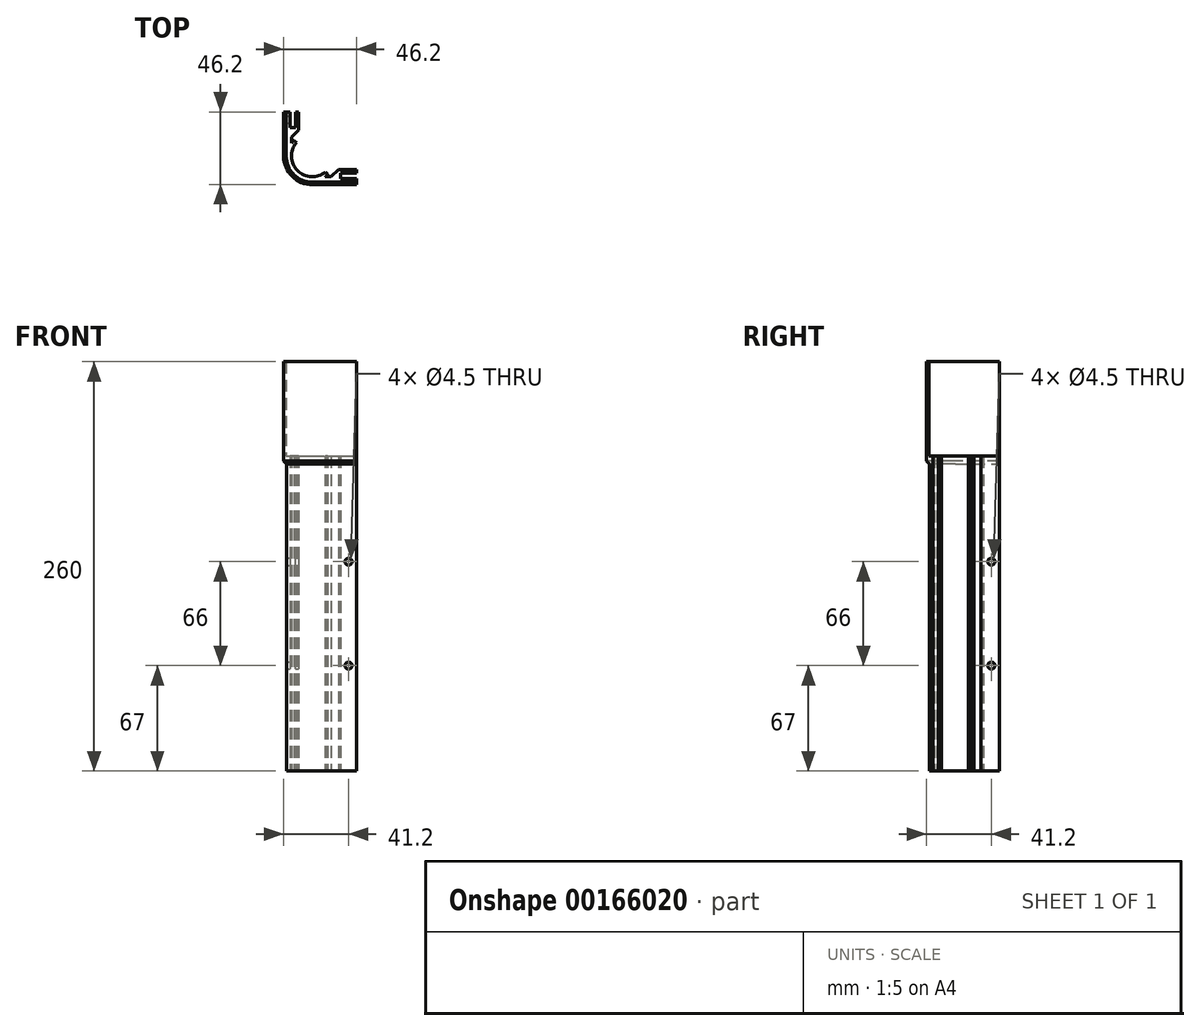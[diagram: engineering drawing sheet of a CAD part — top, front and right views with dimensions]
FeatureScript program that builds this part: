
annotation { "Feature Type Name" : "Feature", "Feature Type Description" : "" }
export const myFeature = defineFeature(function(context is Context, id is Id, definition is map)
    precondition{}
    {
        {
            var Q0;
            Q0=qCreatedBy(makeId("Top.planeOp"),FACE);
            var sketch = newSketch(context, id + "F0", { "sketchPlane" : qUnion([Q0])});
            skCircle(sketch, "E0", {"center": v(0, 0) * mm, "radius": 13.2 * mm, "construction": true});
            skArc(sketch, "E1", {"start": v(-16.2, 0) * mm, "mid": v(-11.46, -11.46) * mm, "end": v(0, -16.2) * mm});
            skLineSegment(sketch, "E2", {"start": v(-5.38, 20.06) * mm, "end": v(5.38, -20.06) * mm, "construction": true});
            skLineSegment(sketch, "E3", {"start": v(21.9, -5.87) * mm, "end": v(-21.9, 5.87) * mm, "construction": true});
            skPoint(sketch, "E4", {"position": v(-3.42, 12.75) * mm});
            skPoint(sketch, "E5", {"position": v(12.75, -3.42) * mm});
            skArc(sketch, "E6", {"start": v(0, -16.2) * mm, "mid": v(9.03, -12.45) * mm, "end": v(12.75, -3.42) * mm});
            skArc(sketch, "E7", {"start": v(-3.42, 12.75) * mm, "mid": v(-9.33, -9.33) * mm, "end": v(12.75, -3.42) * mm});
            skPoint(sketch, "E8", {"position": v(-13.2, 0) * mm});
            skPoint(sketch, "E9", {"position": v(0, -13.2) * mm});
            skArc(sketch, "E10", {"start": v(-16.2, 0) * mm, "mid": v(-12.45, 9.03) * mm, "end": v(-3.42, 12.75) * mm});
            skPoint(sketch, "E11", {"position": v(-11.46, -11.46) * mm});
            skLineSegment(sketch, "E12", {"start": v(-13.2, 0) * mm, "end": v(-13.2, 12) * mm});
            skLineSegment(sketch, "E13", {"start": v(-16.2, 0) * mm, "end": v(-16.2, 12) * mm});
            skLineSegment(sketch, "E14", {"start": v(0, -13.2) * mm, "end": v(12, -13.2) * mm});
            skLineSegment(sketch, "E15", {"start": v(0, -16.2) * mm, "end": v(12, -16.2) * mm});
            skLineSegment(sketch, "E16", {"start": v(-16.2, 12) * mm, "end": v(-16.2, 28) * mm});
            skLineSegment(sketch, "E17", {"start": v(-16.2, 28) * mm, "end": v(-14.2, 28) * mm});
            skLineSegment(sketch, "E18", {"start": v(-13.2, 12) * mm, "end": v(-8.7, 16.5) * mm});
            skLineSegment(sketch, "E19", {"start": v(-8.7, 16.5) * mm, "end": v(-8.7, 28) * mm});
            skLineSegment(sketch, "E20", {"start": v(-8.7, 28) * mm, "end": v(-10.7, 28) * mm});
            skLineSegment(sketch, "E21", {"start": v(-10.7, 28) * mm, "end": v(-10.7, 18) * mm});
            skLineSegment(sketch, "E22", {"start": v(-10.7, 18) * mm, "end": v(-14.2, 18) * mm});
            skLineSegment(sketch, "E23", {"start": v(-14.2, 18) * mm, "end": v(-14.2, 28) * mm});
            skLineSegment(sketch, "E24", {"start": v(0, 0) * mm, "end": v(-11.46, -11.46) * mm, "construction": true});
            skLineSegment(sketch, "E25.MirrorCS", {"start": v(12, -13.2) * mm, "end": v(16.5, -8.7) * mm});
            skLineSegment(sketch, "E26.MirrorCS", {"start": v(16.5, -8.7) * mm, "end": v(28, -8.7) * mm});
            skLineSegment(sketch, "E27.MirrorCS", {"start": v(28, -8.7) * mm, "end": v(28, -10.7) * mm});
            skLineSegment(sketch, "E28.MirrorCS", {"start": v(28, -10.7) * mm, "end": v(18, -10.7) * mm});
            skLineSegment(sketch, "E29.MirrorCS", {"start": v(18, -10.7) * mm, "end": v(18, -14.2) * mm});
            skLineSegment(sketch, "E30.MirrorCS", {"start": v(18, -14.2) * mm, "end": v(28, -14.2) * mm});
            skLineSegment(sketch, "E31.MirrorCS", {"start": v(28, -16.2) * mm, "end": v(28, -14.2) * mm});
            skLineSegment(sketch, "E32.MirrorCS", {"start": v(12, -16.2) * mm, "end": v(28, -16.2) * mm});
            skLineSegment(sketch, "E33", {"start": v(-10.7, 18) * mm, "end": v(15.7, 18) * mm, "construction": true});
            skLineSegment(sketch, "E34", {"start": v(0, 0) * mm, "end": v(0, 18) * mm, "construction": true});
            skSolve(sketch);
        }
        {
            var Q0;
            Q0 = qSketchRegion(id + "F0", true);
            extrude(context, id + "F1", {"entities" : qUnion([Q0]), "depth" : 200 * mm});
        }
        {
            var Q0;
            Q0=makeQuery(id+"F1.opExtrude","SWEPT_EDGE",EDGE,{"disambiguationData":[OSD([sQuery(id+"F0.wireOp",EDGE,"E7"),sQuery(id+"F0.wireOp",EDGE,"E10")])]});
            var Q1;
            Q1=makeQuery(id+"F1.opExtrude","SWEPT_EDGE",EDGE,{"disambiguationData":[OSD([sQuery(id+"F0.wireOp",EDGE,"E6"),sQuery(id+"F0.wireOp",EDGE,"E7")])]});
            chamfer(context, id + "F2", {"entities" : qUnion([Q0, Q1]), "width" : 1 * mm, "tangentPropagation" : true});
        }
        {
            var Q0;
            Q0=makeQuery(id+"F1.opExtrude","CAP_FACE",FACE,{"disambiguationData":[OSD([sQuery(id+"F0.wireOp",EDGE,"E1"),sQuery(id+"F0.wireOp",EDGE,"E6"),sQuery(id+"F0.wireOp",EDGE,"E7"),sQuery(id+"F0.wireOp",EDGE,"E10"),sQuery(id+"F0.wireOp",EDGE,"E12"),sQuery(id+"F0.wireOp",EDGE,"E13"),sQuery(id+"F0.wireOp",EDGE,"E14"),sQuery(id+"F0.wireOp",EDGE,"E15"),sQuery(id+"F0.wireOp",EDGE,"E16"),sQuery(id+"F0.wireOp",EDGE,"E17"),sQuery(id+"F0.wireOp",EDGE,"E18"),sQuery(id+"F0.wireOp",EDGE,"E19"),sQuery(id+"F0.wireOp",EDGE,"E20"),sQuery(id+"F0.wireOp",EDGE,"E21"),sQuery(id+"F0.wireOp",EDGE,"E22"),sQuery(id+"F0.wireOp",EDGE,"E23"),sQuery(id+"F0.wireOp",EDGE,"E25.MirrorCS"),sQuery(id+"F0.wireOp",EDGE,"E26.MirrorCS"),sQuery(id+"F0.wireOp",EDGE,"E27.MirrorCS"),sQuery(id+"F0.wireOp",EDGE,"E28.MirrorCS"),sQuery(id+"F0.wireOp",EDGE,"E29.MirrorCS"),sQuery(id+"F0.wireOp",EDGE,"E30.MirrorCS"),sQuery(id+"F0.wireOp",EDGE,"E31.MirrorCS"),sQuery(id+"F0.wireOp",EDGE,"E32.MirrorCS")])],"isStart":false});
            var sketch = newSketch(context, id + "F3", { "sketchPlane" : qUnion([Q0])});
            skLineSegment(sketch, "E35", {"start": v(28, -16.2) * mm, "end": v(28, -18.2) * mm});
            skPoint(sketch, "E35.endSnap0", {"position": v(28, -15.2) * mm});
            skLineSegment(sketch, "E36", {"start": v(28, -18.2) * mm, "end": v(0, -18.2) * mm});
            skLineSegment(sketch, "E37", {"start": v(-16.2, 28) * mm, "end": v(-18.2, 28) * mm});
            skLineSegment(sketch, "E38", {"start": v(-18.2, 28) * mm, "end": v(-18.2, 0) * mm});
            skArc(sketch, "E39", {"start": v(0, -18.2) * mm, "mid": v(-12.87, -12.87) * mm, "end": v(-18.2, 0) * mm});
            skLineSegment(sketch, "E40.0", {"start": v(-16.7, 0) * mm, "end": v(-16.7, 28) * mm});
            skArc(sketch, "E40.1", {"start": v(-16.7, 0) * mm, "mid": v(-11.8, -11.8) * mm, "end": v(0, -16.7) * mm});
            skLineSegment(sketch, "E40.2", {"start": v(0, -16.7) * mm, "end": v(28, -16.7) * mm});
            skSolve(sketch);
        }
        {
            var Q0;
            Q0=makeQuery(id+"F3.imprint","IMPRINT",FACE,{"disambiguationData":[TD([[makeQuery(id+"F3.imprint","IMPRINT",EDGE,{"derivedFrom":sQuery(id+"F3.wireOp",EDGE,"E35")}),-1.0]])]});
            extrude(context, id + "F4", {"entities" : qUnion([Q0]), "operationType" : NewBodyOperationType.ADD, "oppositeDirection" : true, "depth" : 5 * mm});
        }
        {
            var Q0;
            Q0=makeQuery(id+"F4.opExtrude","CAP_EDGE",EDGE,{"disambiguationData":[OSD([sQuery(id+"F0.wireOp",EDGE,"E13"),sQuery(id+"F0.wireOp",EDGE,"E16")])],"isStart":true});
            var Q1;
            Q1=makeQuery(id+"F4.opExtrude","CAP_EDGE",EDGE,{"disambiguationData":[OSD([sQuery(id+"F3.wireOp",EDGE,"E38")])],"isStart":false});
            chamfer(context, id + "F5", {"entities" : qUnion([Q0, Q1]), "width" : 2 * mm, "tangentPropagation" : true});
        }
        {
            var Q0;
            Q0 = qSketchRegion(id + "F3", true);
            extrude(context, id + "F6", {"entities" : qUnion([Q0]), "operationType" : NewBodyOperationType.ADD, "depth" : 60 * mm});
        }
        {
            var Q0;
            Q0=makeQuery(id+"F1.opExtrude","SWEPT_FACE",FACE,{"disambiguationData":[OSD([sQuery(id+"F0.wireOp",EDGE,"E30.MirrorCS")])]});
            var sketch = newSketch(context, id + "F7", { "sketchPlane" : qUnion([Q0])});
            skLineSegment(sketch, "E41", {"start": v(-23, 200) * mm, "end": v(-23, 0) * mm, "construction": true});
            skCircle(sketch, "E42", {"center": v(-23, 133) * mm, "radius": 2.25 * mm});
            skCircle(sketch, "E43", {"center": v(-23, 67) * mm, "radius": 2.25 * mm});
            skSolve(sketch);
        }
        {
            var Q0;
            Q0 = qSketchRegion(id + "F7", true);
            extrude(context, id + "F8", {"entities" : qUnion([Q0]), "operationType" : NewBodyOperationType.REMOVE, "oppositeDirection" : true, "depth" : 25 * mm, "hasSecondDirection" : true, "secondDirectionOppositeDirection" : false, "secondDirectionDepth" : 25 * mm});
        }
        {
            var Q0;
            Q0=makeQuery(id+"F1.opExtrude","SWEPT_FACE",FACE,{"disambiguationData":[OSD([sQuery(id+"F0.wireOp",EDGE,"E23")])]});
            var sketch = newSketch(context, id + "F9", { "sketchPlane" : qUnion([Q0])});
            skLineSegment(sketch, "E44", {"start": v(23, 200) * mm, "end": v(23, 0) * mm, "construction": true});
            skCircle(sketch, "E45", {"center": v(23, 133) * mm, "radius": 2.25 * mm});
            skCircle(sketch, "E46", {"center": v(23, 67) * mm, "radius": 2.25 * mm});
            skPoint(sketch, "E47", {"position": v(23, 200) * mm});
            skSolve(sketch);
        }
        {
            var Q0;
            Q0 = qSketchRegion(id + "F9", true);
            extrude(context, id + "F10", {"entities" : qUnion([Q0]), "operationType" : NewBodyOperationType.REMOVE, "oppositeDirection" : true, "depth" : 25 * mm, "hasSecondDirection" : true, "secondDirectionOppositeDirection" : false, "secondDirectionDepth" : 25 * mm});
        }
    });
